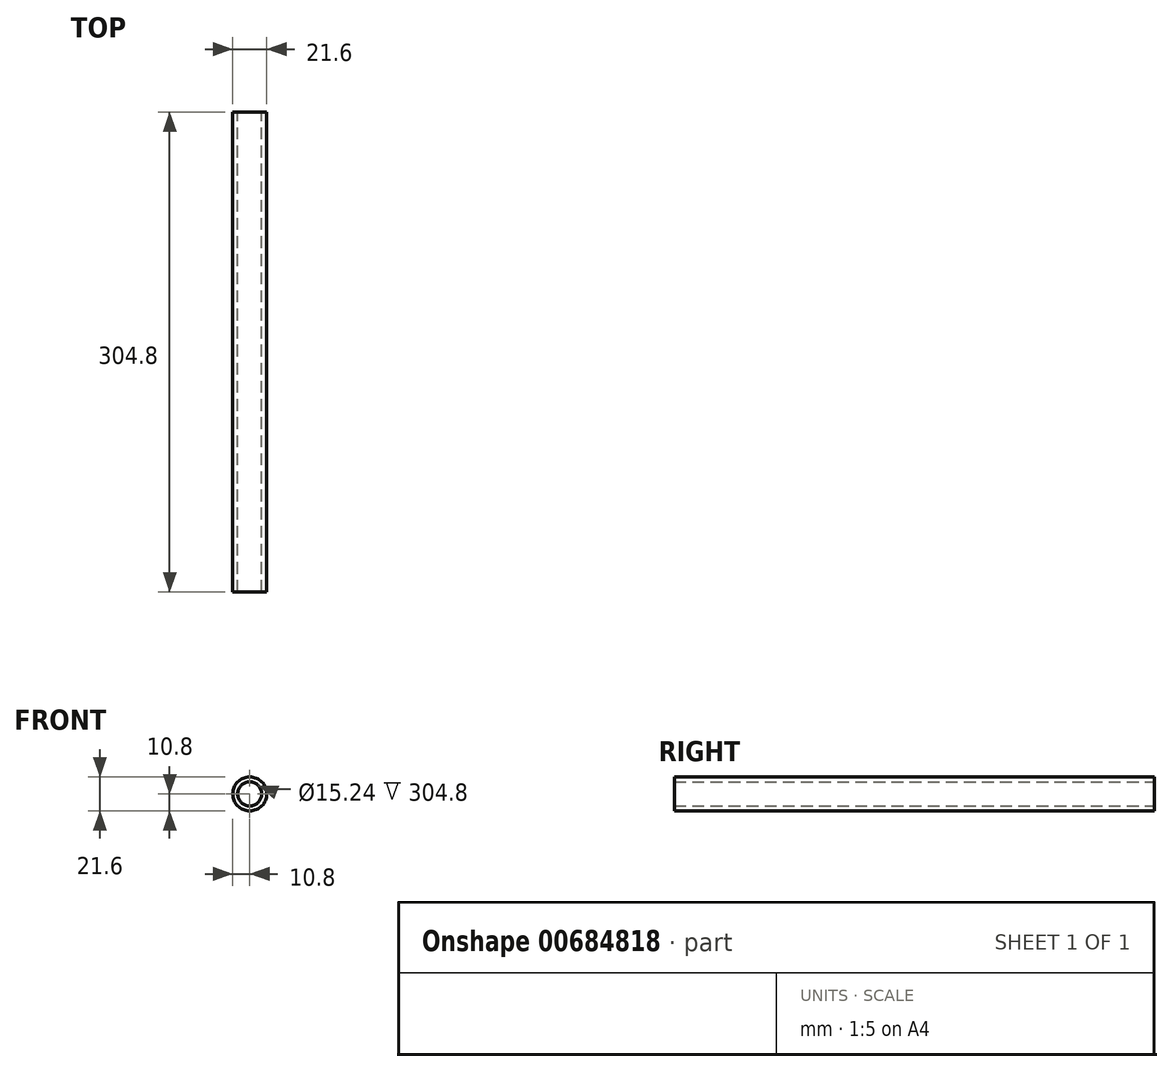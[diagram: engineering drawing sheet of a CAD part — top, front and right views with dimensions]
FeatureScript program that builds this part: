
annotation { "Feature Type Name" : "Feature", "Feature Type Description" : "" }
export const myFeature = defineFeature(function(context is Context, id is Id, definition is map)
    precondition{}
    {
        {
            var Q0;
            Q0=qCreatedBy(makeId("Front.planeOp"),FACE);
            var sketch = newSketch(context, id + "F0", { "sketchPlane" : qUnion([Q0])});
            skCircle(sketch, "E0", {"center": v(0, 0) * mm, "radius": 10.8 * mm});
            skCircle(sketch, "E1", {"center": v(0, 0) * mm, "radius": 7.62 * mm});
            skSolve(sketch);
        }
        {
            var Q0;
            Q0=makeQuery(id+"F0.imprint","IMPRINT",FACE,{"disambiguationData":[TD([[makeQuery(id+"F0.imprint","IMPRINT",EDGE,{"derivedFrom":sQuery(id+"F0.wireOp",EDGE,"E0")}),1.0]])]});
            extrude(context, id + "F1", {"entities" : qUnion([Q0]), "depth" : 304.8 * mm, "offsetDistance" : 25.4 * mm});
        }
    });
